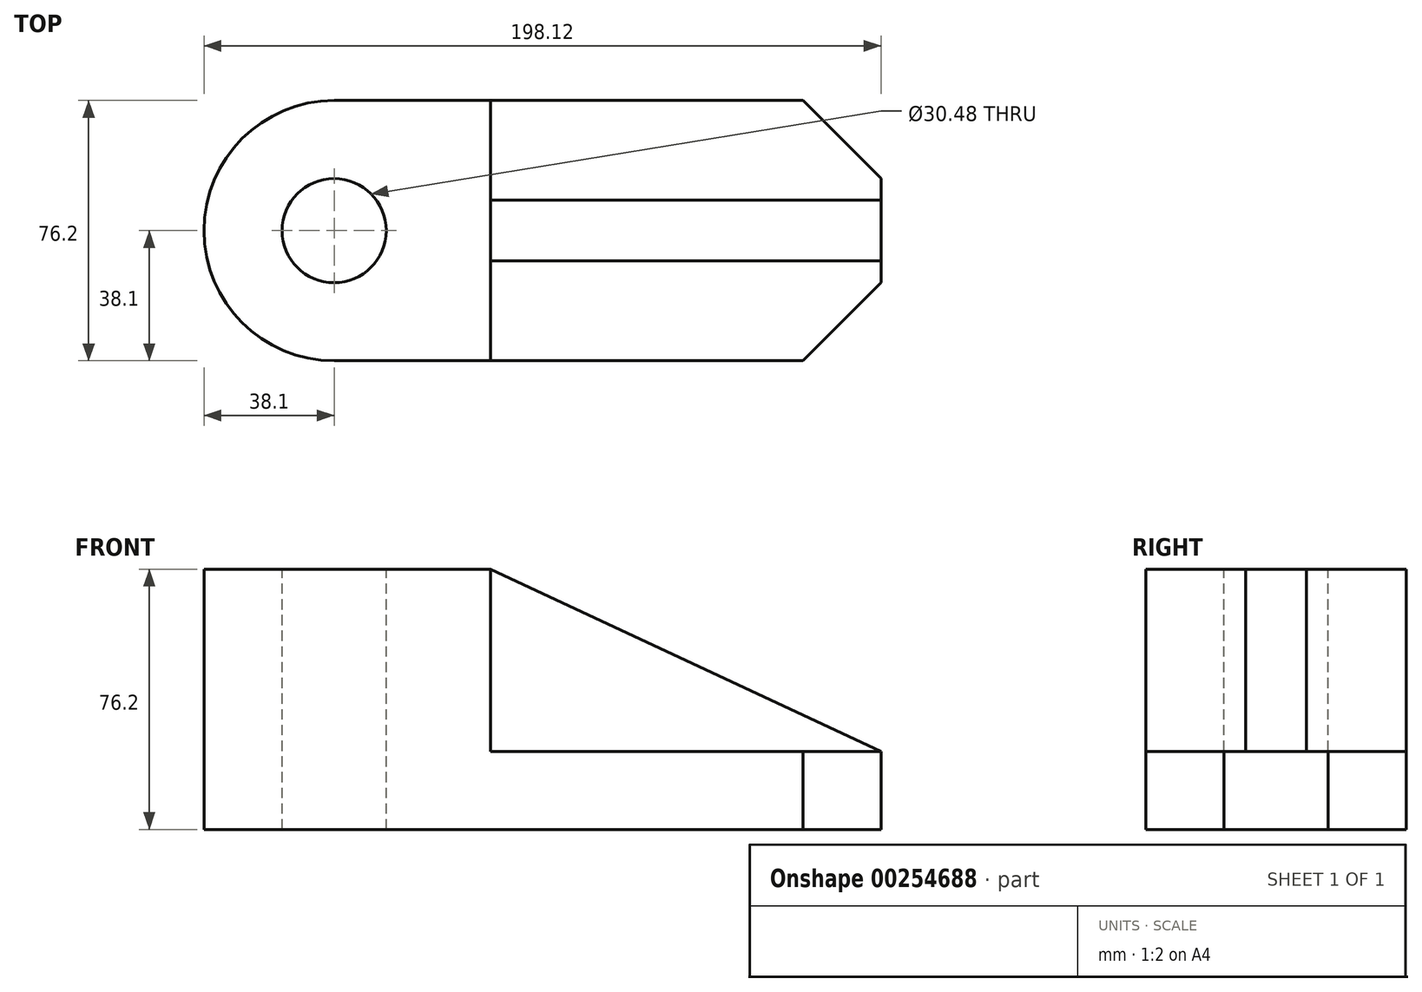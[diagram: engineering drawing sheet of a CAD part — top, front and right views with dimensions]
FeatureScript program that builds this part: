
annotation { "Feature Type Name" : "Feature", "Feature Type Description" : "" }
export const myFeature = defineFeature(function(context is Context, id is Id, definition is map)
    precondition{}
    {
        {
            var Q0;
            Q0=qCreatedBy(makeId("Top.planeOp"),FACE);
            var sketch = newSketch(context, id + "F0", { "sketchPlane" : qUnion([Q0])});
            skLineSegment(sketch, "E0.bottom", {"start": v(38.1, 0) * mm, "end": v(198.12, 0) * mm});
            skLineSegment(sketch, "E0.top", {"start": v(38.1, 76.2) * mm, "end": v(198.12, 76.2) * mm});
            skLineSegment(sketch, "E0.left", {"start": v(0, 38.1) * mm, "end": v(0, 38.1) * mm});
            skLineSegment(sketch, "E0.right", {"start": v(198.12, 0) * mm, "end": v(198.12, 76.2) * mm});
            skPoint(sketch, "E1.visualSharp", {"position": v(0, 76.2) * mm});
            skArc(sketch, "E1.filletArc", {"start": v(38.1, 76.2) * mm, "mid": v(11.16, 65.04) * mm, "end": v(0, 38.1) * mm});
            skPoint(sketch, "E2.visualSharp", {"position": v(0, 0) * mm});
            skArc(sketch, "E2.filletArc", {"start": v(0, 38.1) * mm, "mid": v(11.16, 11.16) * mm, "end": v(38.1, 0) * mm});
            skSolve(sketch);
        }
        {
            var Q0;
            Q0=makeQuery(id+"F0.imprint","IMPRINT",FACE,{"disambiguationData":[TD([[makeQuery(id+"F0.imprint","IMPRINT",EDGE,{"derivedFrom":sQuery(id+"F0.wireOp",EDGE,"E0.bottom")}),1.0]])]});
            extrude(context, id + "F1", {"entities" : qUnion([Q0]), "depth" : 76.2 * mm});
        }
        {
            var Q0;
            Q0=makeQuery(id+"F1.opExtrude","CAP_FACE",FACE,{"disambiguationData":[OSD([sQuery(id+"F0.wireOp",EDGE,"E0.bottom"),sQuery(id+"F0.wireOp",EDGE,"E0.top"),sQuery(id+"F0.wireOp",EDGE,"E0.right"),sQuery(id+"F0.wireOp",EDGE,"E1.filletArc"),sQuery(id+"F0.wireOp",EDGE,"E2.filletArc")])],"isStart":false});
            var sketch = newSketch(context, id + "F2", { "sketchPlane" : qUnion([Q0])});
            skPoint(sketch, "E3", {"position": v(38.1, 38.1) * mm});
            skLineSegment(sketch, "E4", {"start": v(83.82, 0) * mm, "end": v(83.82, 76.2) * mm});
            skLineSegment(sketch, "E5", {"start": v(83.82, 38.1) * mm, "end": v(198.12, 38.1) * mm, "construction": true});
            skLineSegment(sketch, "E6", {"start": v(83.82, 46.99) * mm, "end": v(198.12, 46.99) * mm});
            skLineSegment(sketch, "E7.MirrorCS", {"start": v(83.82, 29.2) * mm, "end": v(198.12, 29.2) * mm});
            skSolve(sketch);
        }
        {
            var Q0;
            Q0=sQuery(id+"F2.wireOp",VERTEX,"E3");
            var Q1;
            Q1=makeQuery(id+"F1.opExtrude","SWEPT_BODY",BODY,{"disambiguationData":[OSD([sQuery(id+"F0.wireOp",EDGE,"E0.bottom"),sQuery(id+"F0.wireOp",EDGE,"E0.top"),sQuery(id+"F0.wireOp",EDGE,"E0.right"),sQuery(id+"F0.wireOp",EDGE,"E1.filletArc"),sQuery(id+"F0.wireOp",EDGE,"E2.filletArc")])]});
            hole(context, id + "F3", {"style" : HoleStyle.SIMPLE, "endStyle" : HoleEndStyle.THROUGH, "holeDiameter" : 30.48 * mm, "tappedDepth" : 12.7 * mm, "tapClearance" : 3, "locations" : qUnion([Q0]), "scope" : qUnion([Q1])});
        }
        {
            var Q0;
            {var subQ3=sQuery(id+"F2.wireOp",EDGE,"E6");Q0=makeQuery(id+"F2.imprint","IMPRINT",FACE,{"disambiguationData":[TD([[makeQuery(id+"F2.imprint","IMPRINT",EDGE,{"derivedFrom":subQ3}),1.0]])]});}
            var Q1;
            {var subQ3=sQuery(id+"F2.wireOp",EDGE,"E7.MirrorCS");Q1=makeQuery(id+"F2.imprint","IMPRINT",FACE,{"disambiguationData":[TD([[makeQuery(id+"F2.imprint","IMPRINT",EDGE,{"derivedFrom":subQ3}),-1.0]])]});}
            extrude(context, id + "F4", {"entities" : qUnion([Q0, Q1]), "operationType" : NewBodyOperationType.REMOVE, "oppositeDirection" : true, "depth" : 53.34 * mm});
        }
        {
            var Q0;
            Q0=makeQuery(id+"F4.boolean.opBoolean","COPY",FACE,{"derivedFrom":makeQuery(id+"F4.opExtrude","SWEPT_FACE",FACE,{"disambiguationData":[OSD([sQuery(id+"F2.wireOp",EDGE,"E7.MirrorCS")])]})});
            var sketch = newSketch(context, id + "F5", { "sketchPlane" : qUnion([Q0])});
            skLineSegment(sketch, "E8", {"start": v(83.82, 76.2) * mm, "end": v(198.12, 22.86) * mm});
            skSolve(sketch);
        }
        {
            var Q0;
            Q0=makeQuery(id+"F5.imprint","IMPRINT",FACE,{"disambiguationData":[TD([[makeQuery(id+"F5.imprint","IMPRINT",EDGE,{"derivedFrom":sQuery(id+"F5.wireOp",EDGE,"E8")}),1.0]])]});
            extrude(context, id + "F6", {"entities" : qUnion([Q0]), "operationType" : NewBodyOperationType.REMOVE, "oppositeDirection" : true, "depth" : 17.78 * mm});
        }
        {
            var Q0;
            Q0=makeQuery(id+"F1.opExtrude","CAP_FACE",FACE,{"disambiguationData":[OSD([sQuery(id+"F0.wireOp",EDGE,"E0.bottom"),sQuery(id+"F0.wireOp",EDGE,"E0.top"),sQuery(id+"F0.wireOp",EDGE,"E0.right"),sQuery(id+"F0.wireOp",EDGE,"E1.filletArc"),sQuery(id+"F0.wireOp",EDGE,"E2.filletArc")])],"isStart":true});
            var sketch = newSketch(context, id + "F7", { "sketchPlane" : qUnion([Q0])});
            skLineSegment(sketch, "E9", {"start": v(0, -38.1) * mm, "end": v(198.12, -38.1) * mm, "construction": true});
            skLineSegment(sketch, "E10", {"start": v(175.26, 0) * mm, "end": v(198.12, -22.86) * mm});
            skLineSegment(sketch, "E11.MirrorCS", {"start": v(175.26, -76.2) * mm, "end": v(198.12, -53.34) * mm});
            skSolve(sketch);
        }
        {
            var Q0;
            {var subQ0=sQuery(id+"F7.wireOp",EDGE,"E10");Q0=makeQuery(id+"F7.imprint","IMPRINT",FACE,{"disambiguationData":[TD([[makeQuery(id+"F7.imprint","IMPRINT",EDGE,{"derivedFrom":subQ0}),1.0]])]});}
            var Q1;
            {var subQ0=sQuery(id+"F7.wireOp",EDGE,"E11.MirrorCS");Q1=makeQuery(id+"F7.imprint","IMPRINT",FACE,{"disambiguationData":[TD([[makeQuery(id+"F7.imprint","IMPRINT",EDGE,{"derivedFrom":subQ0}),-1.0]])]});}
            extrude(context, id + "F8", {"entities" : qUnion([Q0, Q1]), "operationType" : NewBodyOperationType.REMOVE, "oppositeDirection" : true, "depth" : 22.86 * mm});
        }
    });
